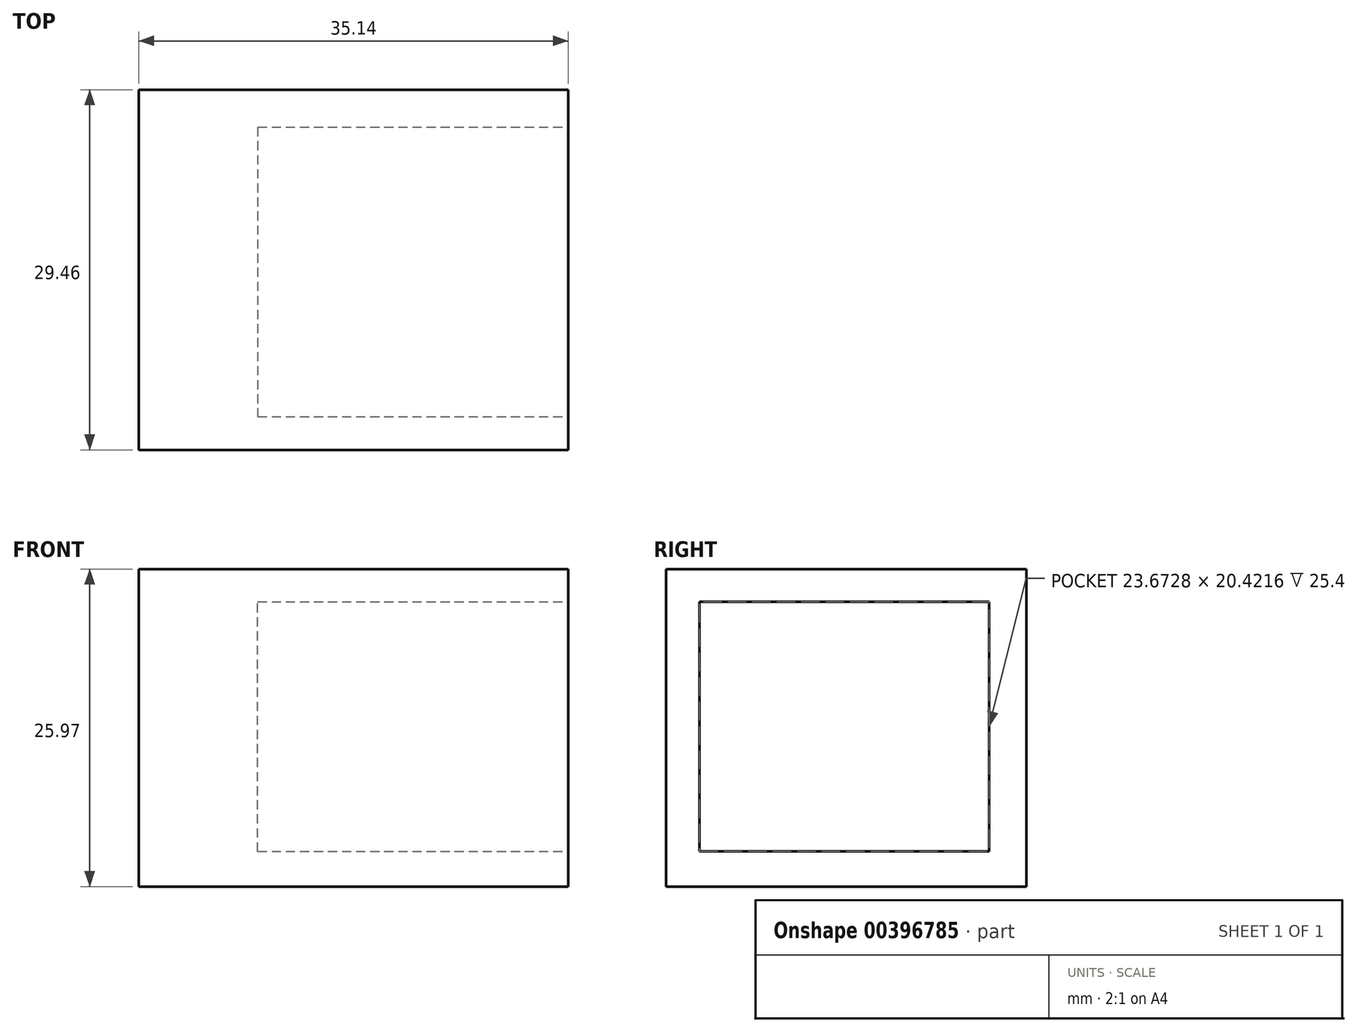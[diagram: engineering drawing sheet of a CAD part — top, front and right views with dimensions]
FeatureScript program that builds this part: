
annotation { "Feature Type Name" : "Feature", "Feature Type Description" : "" }
export const myFeature = defineFeature(function(context is Context, id is Id, definition is map)
    precondition{}
    {
        {
            var Q0;
            Q0=qCreatedBy(makeId("Front.planeOp"),FACE);
            var sketch = newSketch(context, id + "F0", { "sketchPlane" : qUnion([Q0])});
            skLineSegment(sketch, "E0.bottom", {"start": v(0, 0) * mm, "end": v(-35.14, 0) * mm});
            skLineSegment(sketch, "E0.top", {"start": v(0, 25.97) * mm, "end": v(-35.14, 25.97) * mm});
            skLineSegment(sketch, "E0.left", {"start": v(0, 0) * mm, "end": v(0, 25.97) * mm});
            skLineSegment(sketch, "E0.right", {"start": v(-35.14, 0) * mm, "end": v(-35.14, 25.97) * mm});
            skSolve(sketch);
        }
        {
            var Q0;
            Q0=makeQuery(id+"F0.imprint","IMPRINT",FACE,{"disambiguationData":[TD([[makeQuery(id+"F0.imprint","IMPRINT",EDGE,{"derivedFrom":sQuery(id+"F0.wireOp",EDGE,"E0.bottom")}),-1.0]])]});
            extrude(context, id + "F1", {"entities" : qUnion([Q0]), "depth" : 29.46 * mm});
        }
        {
            var Q0;
            Q0=makeQuery(id+"F1.opExtrude","SWEPT_FACE",FACE,{"disambiguationData":[OSD([sQuery(id+"F0.wireOp",EDGE,"E0.left")])]});
            var sketch = newSketch(context, id + "F2", { "sketchPlane" : qUnion([Q0])});
            skLineSegment(sketch, "E1.bottom", {"start": v(-3.06, 2.86) * mm, "end": v(-26.73, 2.86) * mm});
            skLineSegment(sketch, "E1.top", {"start": v(-3.06, 23.29) * mm, "end": v(-26.73, 23.29) * mm});
            skLineSegment(sketch, "E1.left", {"start": v(-3.06, 2.86) * mm, "end": v(-3.06, 23.29) * mm});
            skLineSegment(sketch, "E1.right", {"start": v(-26.73, 2.86) * mm, "end": v(-26.73, 23.29) * mm});
            skSolve(sketch);
        }
        {
            var Q0;
            Q0 = qSketchRegion(id + "F2", true);
            extrude(context, id + "F3", {"entities" : qUnion([Q0]), "operationType" : NewBodyOperationType.REMOVE, "oppositeDirection" : true, "depth" : 25.4 * mm});
        }
    });
